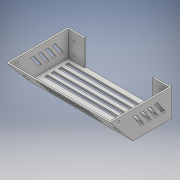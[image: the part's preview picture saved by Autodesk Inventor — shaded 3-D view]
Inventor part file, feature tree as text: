
AUTODESK INVENTOR PART (.ipt)
format: ipt  version: 2018.2 (Build 222227000, 227)  size: 333,824 bytes
history: native  units: mm
features: extrude x12, sketch x11, plane x1
ambient origin geometry x8: Origin, YZ Plane, XZ Plane, XY Plane, X Axis, Y Axis, Z Axis, Center Point
bodies: Solid1 (feature_tree)
feature tree (24):
  extrude  "Extrusion1"  Depth=60.0mm
  extrude  "Extrusion2"  Depth=5.0mm
  extrude  "Extrusion3"  Depth=5.0mm
  extrude  "Extrusion4"  Depth=2.4mm TaperAngle=0.0deg
  extrude  "Extrusion5"  Depth=2.4mm
  sketch  "Sketch6"  dims[d11=39.6mm d12=0.0mm d13=24.43461mm]
  plane  "Work Plane1"
  extrude  "Extrusion8"  Depth=39.6mm
  extrude  "Extrusion9"  Depth=2.4mm TaperAngle=0.0deg
  extrude  "Extrusion10"  Depth=157.6mm TaperAngle=0.0deg
  extrude  "Extrusion11"  Depth=5.0mm
  extrude  "Extrusion12"  Depth=5.0mm
  sketch  "Sketch11"  dims[d25=5.0mm d26=6.0mm d27=5.0mm d28=22.0mm d29=5.0mm d30=6.0mm d31=5.0mm d32=6.0mm d33=5.0mm d34=6.0mm d35=5.0mm d36=10.0mm d39=-50.0mm d40=4.0mm d41=4.0mm d42=10.0mm d43=10.0mm d44=20.0mm d45=20.0mm d46=40.0mm d47=4.0mm d49=4.0mm d50=4.0mm d51=4.0mm d52=4.0mm d55=4.0mm d56=80.0mm d57=80.0mm d58=80.0mm d59=80.000202mm d60=80.0mm d61=160.0mm d62=0.0mm d63=4.0mm d64=10.0mm d65=4.0mm d66=10.0mm d67=17.0mm d68=17.0mm d69=160.0mm d70=0.0mm d71=2.4mm d72=25.0mm d73=0.0mm d74=2.4mm d75=25.0mm d76=0.0mm d77=3.0mm d78=7.0mm d79=5.0mm d80=160.0mm d81=0.0mm d82=3.0mm d83=12.5mm d84=12.0mm d85=3.0mm d86=12.5mm d87=12.0mm d88=3.0mm d89=3.0mm d90=12.5mm d91=12.0mm d92=12.0mm d93=12.5mm d94=12.0mm d95=0.0mm d96=7.0mm d97=2.0mm d98=12.5mm d99=12.5mm d101=2.0mm d103=7.0mm d104=12.5mm d105=3.0mm d106=0.0mm d107=12.5mm]
  extrude  "Extrusion13"  Depth=12.5mm
  extrude  "Extrusion14"  Depth=5.0mm
  sketch  "Sketch1"  dims[d0=160.0mm d1=60.0mm]
  sketch  "Sketch2"  dims[d2=140.0mm d3=5.0mm]
  sketch  "Sketch3"  dims[d4=5.0mm d5=5.0mm]
  sketch  "Sketch4"  dims[d6=5.0mm d7=2.4mm d8=0.0mm]
  sketch  "Sketch5"  dims[d9=2.4mm d10=2.4mm]
  sketch  "Sketch7"  dims[d14=2.4mm d15=0.0mm d16=2.4mm d17=0.0mm]
  sketch  "Sketch8"  dims[d18=2.4mm d19=157.6mm d20=0.0mm]
  sketch  "Sketch9"  dims[d21=5.0mm d22=6.0mm]
  sketch  "Sketch10"  dims[d23=5.0mm d24=6.0mm]
